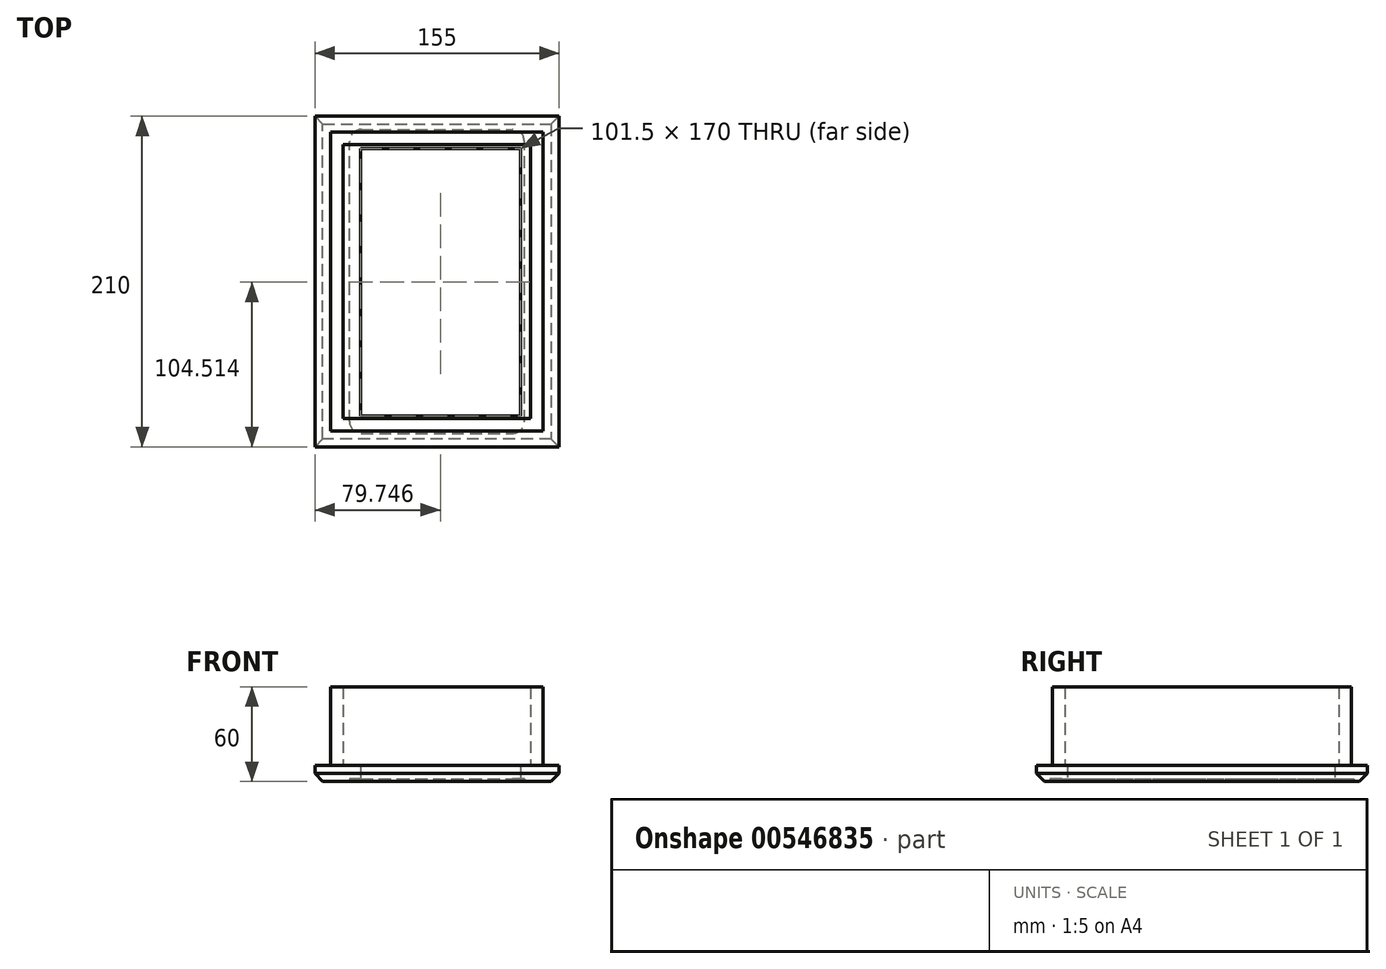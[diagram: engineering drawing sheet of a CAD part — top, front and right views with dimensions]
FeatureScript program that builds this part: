
annotation { "Feature Type Name" : "Feature", "Feature Type Description" : "" }
export const myFeature = defineFeature(function(context is Context, id is Id, definition is map)
    precondition{}
    {
        {
            var Q0;
            Q0=qCreatedBy(makeId("Top.planeOp"),FACE);
            var sketch = newSketch(context, id + "F0", { "sketchPlane" : qUnion([Q0])});
            skLineSegment(sketch, "E0.bottom", {"start": v(-178.8, 88.27) * mm, "end": v(-23.8, 88.27) * mm});
            skLineSegment(sketch, "E0.top", {"start": v(-178.8, -121.73) * mm, "end": v(-23.8, -121.73) * mm});
            skLineSegment(sketch, "E0.left", {"start": v(-178.8, 88.27) * mm, "end": v(-178.8, -121.73) * mm});
            skLineSegment(sketch, "E0.right", {"start": v(-23.8, 88.27) * mm, "end": v(-23.8, -121.73) * mm});
            skLineSegment(sketch, "E1.bottom", {"start": v(-168.8, 78.27) * mm, "end": v(-33.8, 78.27) * mm});
            skLineSegment(sketch, "E1.top", {"start": v(-168.8, -111.73) * mm, "end": v(-33.8, -111.73) * mm});
            skLineSegment(sketch, "E1.left", {"start": v(-168.8, 78.27) * mm, "end": v(-168.8, -111.73) * mm});
            skLineSegment(sketch, "E1.right", {"start": v(-33.8, 78.27) * mm, "end": v(-33.8, -111.73) * mm});
            skLineSegment(sketch, "E2.bottom", {"start": v(-160.8, 70.27) * mm, "end": v(-41.8, 70.27) * mm});
            skLineSegment(sketch, "E2.top", {"start": v(-160.8, -103.73) * mm, "end": v(-41.8, -103.73) * mm});
            skLineSegment(sketch, "E2.left", {"start": v(-160.8, 70.27) * mm, "end": v(-160.8, -103.73) * mm});
            skLineSegment(sketch, "E2.right", {"start": v(-41.8, 70.27) * mm, "end": v(-41.8, -103.73) * mm});
            skSolve(sketch);
        }
        {
            var Q0;
            Q0=makeQuery(id+"F0.imprint","IMPRINT",FACE,{"disambiguationData":[TD([[makeQuery(id+"F0.imprint","IMPRINT",EDGE,{"derivedFrom":sQuery(id+"F0.wireOp",EDGE,"E1.bottom")}),-1.0]])]});
            var Q1;
            {var subQ6=sQuery(id+"F0.wireOp",EDGE,"E1.right");Q1=makeQuery(id+"F0.imprint","IMPRINT",FACE,{"disambiguationData":[TD([[makeQuery(id+"F0.imprint","IMPRINT",EDGE,{"derivedFrom":subQ6}),-1.0]])]});}
            var Q2;
            {var subQ7=sQuery(id+"F0.wireOp",EDGE,"a1b0a058-522f-4bee-b554-46a16c6f544b.filletArc");var subQ9=sQuery(id+"F0.wireOp",EDGE,"E1.top");var subQ11=makeQuery(id+"F0.imprint","INTERSECT",VERTEX,{"derivedFrom":[subQ9,subQ7]});Q2=makeQuery(id+"F0.imprint","IMPRINT",FACE,{"disambiguationData":[TD([[makeQuery(id+"F0.imprint","IMPRINT",EDGE,{"disambiguationData":[TD([[subQ11,-1.0]])],"derivedFrom":subQ9}),1.0]])]});}
            var Q3;
            {var subQ0=sQuery(id+"F0.wireOp",EDGE,"E1.left");Q3=makeQuery(id+"F0.imprint","IMPRINT",FACE,{"disambiguationData":[TD([[makeQuery(id+"F0.imprint","IMPRINT",EDGE,{"derivedFrom":subQ0}),1.0]])]});}
            extrude(context, id + "F1", {"entities" : qUnion([Q0, Q1, Q2, Q3]), "depth" : 50 * mm, "offsetDistance" : 25 * mm});
        }
        {
            var Q0;
            Q0 = qSketchRegion(id + "F0", true);
            var Q1;
            Q1=makeQuery(id+"F0.imprint","IMPRINT",FACE,{"disambiguationData":[TD([[makeQuery(id+"F0.imprint","IMPRINT",EDGE,{"derivedFrom":sQuery(id+"F0.wireOp",EDGE,"E1.bottom")}),-1.0]])]});
            var Q2;
            {var subQ5=sQuery(id+"F0.wireOp",EDGE,"uw5mAx07-9u3E-B76H-PSYv-ceBDDvy5iLns.top");Q2=makeQuery(id+"F0.imprint","IMPRINT",FACE,{"disambiguationData":[TD([[makeQuery(id+"F0.imprint","IMPRINT",EDGE,{"derivedFrom":subQ5}),1.0]])]});}
            var Q3;
            {var subQ5=sQuery(id+"F0.wireOp",EDGE,"uw5mAx07-9u3E-B76H-PSYv-ceBDDvy5iLns.bottom");Q3=makeQuery(id+"F0.imprint","IMPRINT",FACE,{"disambiguationData":[TD([[makeQuery(id+"F0.imprint","IMPRINT",EDGE,{"derivedFrom":subQ5}),-1.0]])]});}
            var Q4;
            {var subQ0=sQuery(id+"F0.wireOp",EDGE,"E1.left");Q4=makeQuery(id+"F0.imprint","IMPRINT",FACE,{"disambiguationData":[TD([[makeQuery(id+"F0.imprint","IMPRINT",EDGE,{"derivedFrom":subQ0}),1.0]])]});}
            var Q5;
            {var subQ7=sQuery(id+"F0.wireOp",EDGE,"a1b0a058-522f-4bee-b554-46a16c6f544b.filletArc");var subQ9=sQuery(id+"F0.wireOp",EDGE,"E1.top");var subQ11=makeQuery(id+"F0.imprint","INTERSECT",VERTEX,{"derivedFrom":[subQ9,subQ7]});Q5=makeQuery(id+"F0.imprint","IMPRINT",FACE,{"disambiguationData":[TD([[makeQuery(id+"F0.imprint","IMPRINT",EDGE,{"disambiguationData":[TD([[subQ11,-1.0]])],"derivedFrom":subQ9}),1.0]])]});}
            var Q6;
            {var subQ6=sQuery(id+"F0.wireOp",EDGE,"E1.right");Q6=makeQuery(id+"F0.imprint","IMPRINT",FACE,{"disambiguationData":[TD([[makeQuery(id+"F0.imprint","IMPRINT",EDGE,{"derivedFrom":subQ6}),-1.0]])]});}
            var Q7;
            {var subQ0=sQuery(id+"F0.wireOp",EDGE,"uw5mAx07-9u3E-B76H-PSYv-ceBDDvy5iLns.left");var subQ1=sQuery(id+"F0.wireOp",EDGE,"E2.bottom");var subQ2=makeQuery(id+"F0.imprint","INTERSECT",VERTEX,{"derivedFrom":[subQ1,subQ0]});Q7=makeQuery(id+"F0.imprint","IMPRINT",FACE,{"disambiguationData":[TD([[makeQuery(id+"F0.imprint","IMPRINT",EDGE,{"disambiguationData":[TD([[subQ2,-1.0]])],"derivedFrom":subQ1}),-1.0]])]});}
            var Q8;
            {var subQ0=sQuery(id+"F0.wireOp",EDGE,"E2.right");Q8=makeQuery(id+"F0.imprint","IMPRINT",FACE,{"disambiguationData":[TD([[makeQuery(id+"F0.imprint","IMPRINT",EDGE,{"derivedFrom":subQ0}),-1.0]])]});}
            var Q9;
            {var subQ0=sQuery(id+"F0.wireOp",EDGE,"E2.left");Q9=makeQuery(id+"F0.imprint","IMPRINT",FACE,{"disambiguationData":[TD([[makeQuery(id+"F0.imprint","IMPRINT",EDGE,{"derivedFrom":subQ0}),1.0]])]});}
            extrude(context, id + "F2", {"entities" : qUnion([Q0, Q1, Q2, Q3, Q4, Q5, Q6, Q7, Q8, Q9]), "operationType" : NewBodyOperationType.ADD, "oppositeDirection" : true, "depth" : 10 * mm, "offsetDistance" : 25 * mm});
        }
        {
            var Q0;
            Q0=makeQuery(id+"F2.opExtrude","CAP_EDGE",EDGE,{"disambiguationData":[OSD([sQuery(id+"F0.wireOp",EDGE,"E0.bottom")])],"isStart":false});
            var Q1;
            Q1=makeQuery(id+"F2.opExtrude","CAP_EDGE",EDGE,{"disambiguationData":[OSD([sQuery(id+"F0.wireOp",EDGE,"E0.left")])],"isStart":false});
            var Q2;
            Q2=makeQuery(id+"F2.opExtrude","CAP_EDGE",EDGE,{"disambiguationData":[OSD([sQuery(id+"F0.wireOp",EDGE,"E0.top")])],"isStart":false});
            var Q3;
            Q3=makeQuery(id+"F2.opExtrude","CAP_EDGE",EDGE,{"disambiguationData":[OSD([sQuery(id+"F0.wireOp",EDGE,"E0.right")])],"isStart":false});
            chamfer(context, id + "F3", {"entities" : qUnion([Q0, Q1, Q2, Q3]), "width" : 5 * mm, "tangentPropagation" : true});
        }
        {
            var Q0;
            Q0=makeQuery(id+"F2.opExtrude","CAP_FACE",FACE,{"disambiguationData":[OSD([sQuery(id+"F0.wireOp",EDGE,"E0.bottom"),sQuery(id+"F0.wireOp",EDGE,"E0.top"),sQuery(id+"F0.wireOp",EDGE,"E0.left"),sQuery(id+"F0.wireOp",EDGE,"E0.right")])],"isStart":false});
            var sketch = newSketch(context, id + "F4", { "sketchPlane" : qUnion([Q0])});
            skLineSegment(sketch, "E3.bottom", {"start": v(-149.3, 113.22) * mm, "end": v(-53.3, 113.22) * mm});
            skLineSegment(sketch, "E3.top", {"start": v(-149.3, -79.78) * mm, "end": v(-53.3, -79.78) * mm});
            skLineSegment(sketch, "E3.left", {"start": v(-156.8, 105.72) * mm, "end": v(-156.8, -72.28) * mm});
            skLineSegment(sketch, "E3.right", {"start": v(-45.8, 105.72) * mm, "end": v(-45.8, -72.28) * mm});
            skPoint(sketch, "E4.visualSharp", {"position": v(-156.8, 113.22) * mm});
            skArc(sketch, "E4.filletArc", {"start": v(-149.3, 113.22) * mm, "mid": v(-154.6, 111.02) * mm, "end": v(-156.8, 105.72) * mm});
            skPoint(sketch, "E5.visualSharp", {"position": v(-45.8, 113.22) * mm});
            skArc(sketch, "E5.filletArc", {"start": v(-45.8, 105.72) * mm, "mid": v(-48, 111.02) * mm, "end": v(-53.3, 113.22) * mm});
            skPoint(sketch, "E6.visualSharp", {"position": v(-45.8, -79.78) * mm});
            skArc(sketch, "E6.filletArc", {"start": v(-53.3, -79.78) * mm, "mid": v(-48, -77.59) * mm, "end": v(-45.8, -72.28) * mm});
            skPoint(sketch, "E7.visualSharp", {"position": v(-156.8, -79.78) * mm});
            skArc(sketch, "E7.filletArc", {"start": v(-156.8, -72.28) * mm, "mid": v(-154.6, -77.59) * mm, "end": v(-149.3, -79.78) * mm});
            skSolve(sketch);
        }
        {
            var Q0;
            Q0=makeQuery(id+"F4.imprint","IMPRINT",FACE,{"disambiguationData":[TD([[makeQuery(id+"F4.imprint","IMPRINT",EDGE,{"derivedFrom":sQuery(id+"F4.wireOp",EDGE,"E3.bottom")}),-1.0]])]});
            extrude(context, id + "F5", {"entities" : qUnion([Q0]), "operationType" : NewBodyOperationType.REMOVE, "oppositeDirection" : true, "depth" : 1.5 * mm, "offsetDistance" : 25 * mm});
        }
        {
            var Q0;
            Q0=makeQuery(id+"F4.imprint","IMPRINT",FACE,{"disambiguationData":[TD([[makeQuery(id+"F4.imprint","IMPRINT",EDGE,{"derivedFrom":sQuery(id+"F4.wireOp",EDGE,"E3.bottom")}),1.0]])]});
            var sketch = newSketch(context, id + "F6", { "sketchPlane" : qUnion([Q0])});
            skLineSegment(sketch, "E8.bottom", {"start": v(-149.8, 102.22) * mm, "end": v(-48.3, 102.22) * mm});
            skLineSegment(sketch, "E8.top", {"start": v(-149.8, -67.78) * mm, "end": v(-48.3, -67.78) * mm});
            skLineSegment(sketch, "E8.left", {"start": v(-149.8, 102.22) * mm, "end": v(-149.8, -67.78) * mm});
            skLineSegment(sketch, "E8.right", {"start": v(-48.3, 102.22) * mm, "end": v(-48.3, -67.78) * mm});
            skSolve(sketch);
        }
        {
            var Q0;
            Q0=makeQuery(id+"F6.imprint","IMPRINT",FACE,{"disambiguationData":[TD([[makeQuery(id+"F6.imprint","IMPRINT",EDGE,{"derivedFrom":sQuery(id+"F6.wireOp",EDGE,"E8.bottom")}),-1.0]])]});
            extrude(context, id + "F7", {"entities" : qUnion([Q0]), "operationType" : NewBodyOperationType.REMOVE, "endBound" : BoundingType.THROUGH_ALL, "oppositeDirection" : true, "depth" : 25 * mm, "offsetDistance" : 25 * mm});
        }
    });
